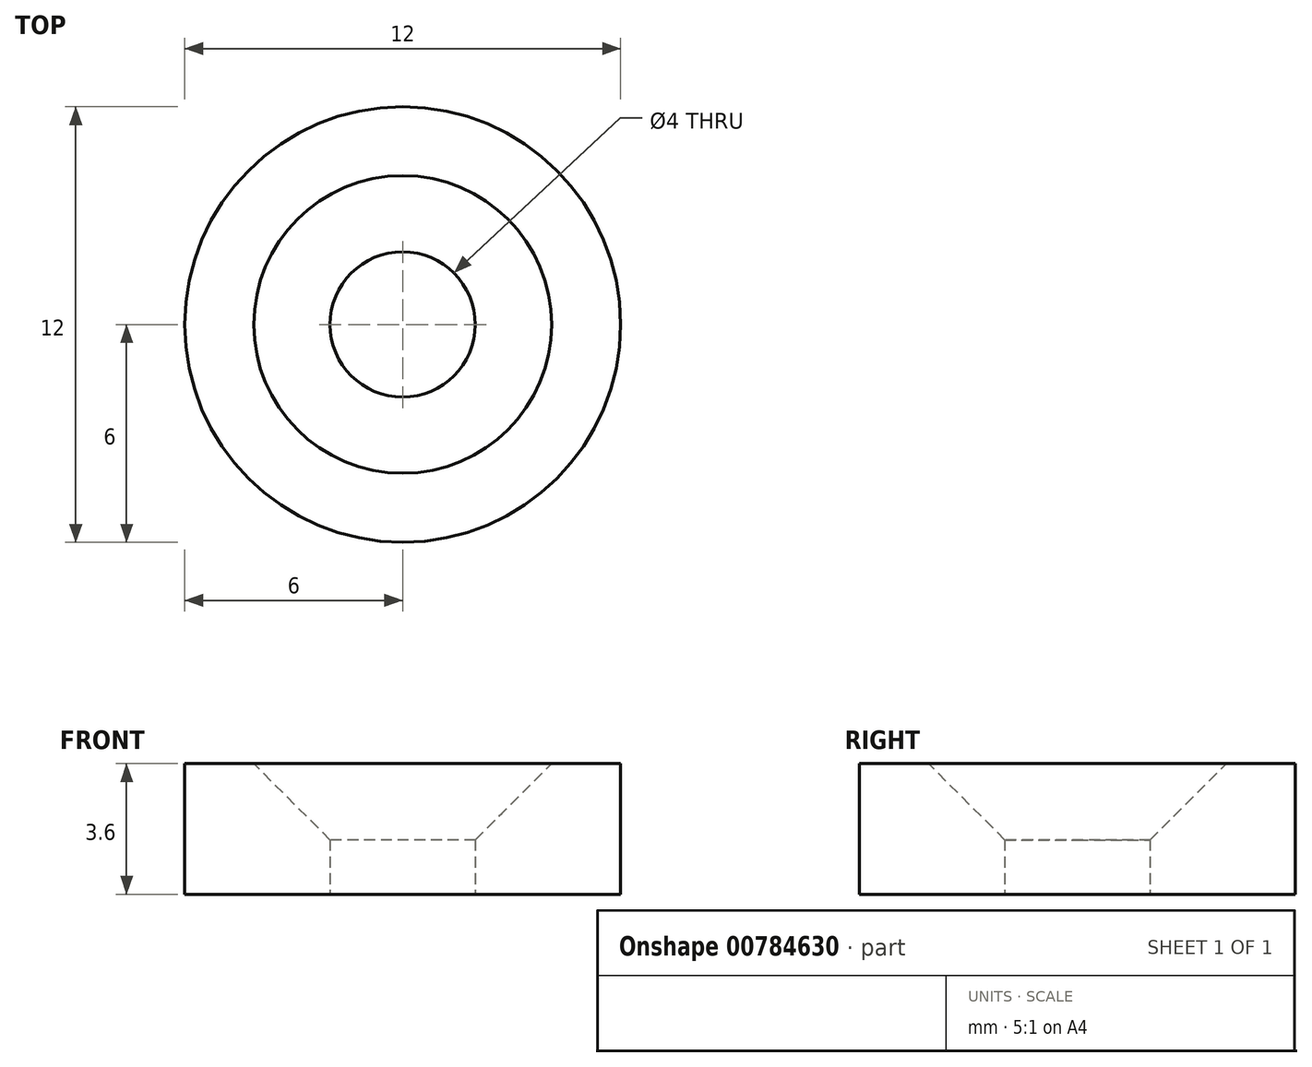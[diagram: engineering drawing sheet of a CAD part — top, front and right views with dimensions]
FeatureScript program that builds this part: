
annotation { "Feature Type Name" : "Feature", "Feature Type Description" : "" }
export const myFeature = defineFeature(function(context is Context, id is Id, definition is map)
    precondition{}
    {
        {
            var Q0;
            Q0=qCreatedBy(makeId("Top.planeOp"),FACE);
            var sketch = newSketch(context, id + "F0", { "sketchPlane" : qUnion([Q0])});
            skCircle(sketch, "E0", {"center": v(0, 0) * mm, "radius": 6 * mm});
            skCircle(sketch, "E1", {"center": v(0, 0) * mm, "radius": 2 * mm});
            skSolve(sketch);
        }
        {
            var Q0;
            Q0 = qSketchRegion(id + "F0", true);
            extrude(context, id + "F1", {"entities" : qUnion([Q0]), "depth" : 3.6 * mm, "offsetDistance" : 25 * mm});
        }
        {
            var Q0;
            Q0=makeQuery(id+"F1.opExtrude","CAP_EDGE",EDGE,{"disambiguationData":[OSD([sQuery(id+"F0.wireOp",EDGE,"E1")])],"isStart":false});
            chamfer(context, id + "F2", {"entities" : qUnion([Q0]), "width" : 2.1 * mm, "tangentPropagation" : true});
        }
        {
            var Q0;
            Q0=qCreatedBy(makeId("Right.planeOp"),FACE);
            var sketch = newSketch(context, id + "F3", { "sketchPlane" : qUnion([Q0])});
            skLineSegment(sketch, "E2", {"start": v(4.1, 3.6) * mm, "end": v(2, 1.5) * mm});
            skLineSegment(sketch, "E3", {"start": v(-2, 1.5) * mm, "end": v(-4.1, 3.6) * mm});
            skLineSegment(sketch, "E4.0", {"start": v(-2, 1.5) * mm, "end": v(2, 1.5) * mm});
            skCircle(sketch, "E5", {"center": v(0, 6.57) * mm, "radius": 5 * mm});
            skSolve(sketch);
        }
    });
